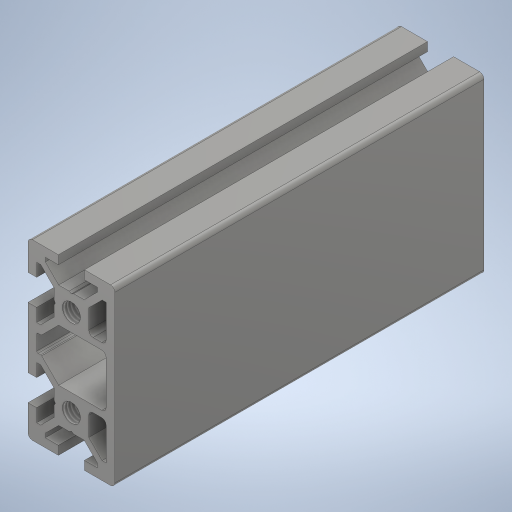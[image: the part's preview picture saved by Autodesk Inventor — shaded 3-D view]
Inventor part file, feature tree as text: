
AUTODESK INVENTOR PART (.ipt)
format: ipt  version: 2024 (Build 280153000, 153)  size: 369,152 bytes
history: native  units: mm
features: other x7, thread x4, sketch x2, extrude x1, hole x1, pattern_linear x1
ambient origin geometry x8: Origin, YZ Plane, XZ Plane, XY Plane, X Axis, Y Axis, Z Axis, Center Point
bodies: Solid1 (feature_tree)
feature tree (16):
  extrude  "Extrusion1"  Depth=20.0mm TaperAngle=0.0deg
  hole  "Hole1"  [1 undecoded]
  pattern_linear  "Rectangular Pattern1"  Spacing1=10.0mm  [1 undecoded]
  other  "C1_XY"
  other  "C1_YZ"
  other  "C1_ZX"
  other  "C1_X"
  other  "C1_Y"
  other  "C1_Z"
  other  "C1_Center"
  thread  "Thread1"  [1 undecoded]
  thread  "Thread2"  [1 undecoded]
  thread  "Thread3"  [1 undecoded]
  thread  "Thread4"  [1 undecoded]
  sketch  "Sketch_63"  dims[d2=4.2mm d3=6.0mm d4=4.0mm d5=2.0mm d6=90.0deg d7=110.0mm d8=0.0mm d9=20.0mm d11=20.0mm d12=10.0mm d14=0.0mm d15=0.0mm d16=10.0mm d17=0.0mm d18=10.0mm d19=0.0mm d20=10.0mm d21=0.0mm d22=10.0mm d23=0.0mm]
  sketch  "Sketch2"  dims[d0=85.0mm d1=0.0mm]
note: 6 required parameter values undecoded (feature->parameter linkage not recoverable at this tier; creation-order binding heuristic only, values carry confidence <= 0.55)
